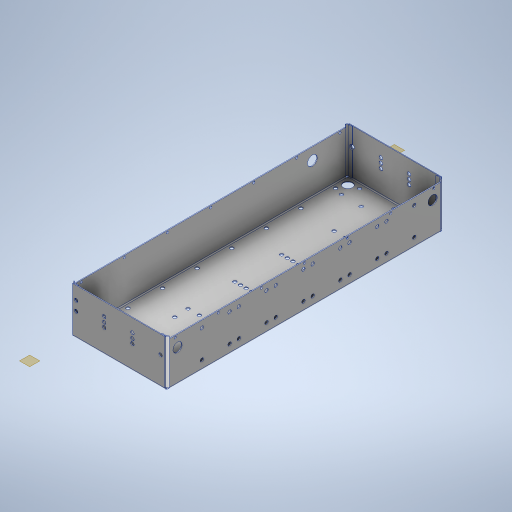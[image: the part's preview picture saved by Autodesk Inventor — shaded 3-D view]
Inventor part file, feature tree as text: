
AUTODESK INVENTOR PART (.ipt)
format: ipt  version: 2023 (Build 270158000, 158)  size: 787,968 bytes
history: native  units: in
note: dims shown in document units (in); Inventor stores cm internally (conversion verified against a paired STEP export)
features: sketch x26, hole x20, sheet_metal_op x12, pattern_linear x12, other x8, plane x4
ambient origin geometry x8: Origin, YZ Plane, XZ Plane, XY Plane, X Axis, Y Axis, Z Axis, Center Point
bodies: Solid1 (feature_tree)
feature tree (82):
  sheet_metal_op  "Face1"
  sheet_metal_op  "Flange1"
  sheet_metal_op  "Flange2"
  sheet_metal_op  "Unfold1"
  hole  "Hole1"  [1 undecoded]
  pattern_linear  "Rectangular Pattern1"  Count1=30  [1 undecoded]
  pattern_linear  "Rectangular Pattern2"  Count1=10  [1 undecoded]
  hole  "Hole2"  [1 undecoded]
  pattern_linear  "Rectangular Pattern3"  Count1=10 Spacing1=90.0deg
  hole  "Hole3"  [1 undecoded]
  hole  "Hole6"  [1 undecoded]
  pattern_linear  "Rectangular Pattern6"  Count1=10 Spacing1=90.0deg
  plane  "Work Plane4"
  hole  "Hole7"  [1 undecoded]
  plane  "Work Plane3"
  hole  "Hole8"  [1 undecoded]
  plane  "Work Plane2"
  hole  "Hole9"  [1 undecoded]
  plane  "Work Plane1"
  hole  "Hole10"  [1 undecoded]
  hole  "Hole11"  [1 undecoded]
  hole  "Hole12"  [1 undecoded]
  hole  "Hole13"  [1 undecoded]
  pattern_linear  "Rectangular Pattern11"  Count1=6  [1 undecoded]
  pattern_linear  "Rectangular Pattern12"  Count1=6  [1 undecoded]
  pattern_linear  "Rectangular Pattern13"  Count1=6  [1 undecoded]
  pattern_linear  "Rectangular Pattern14"  Count1=2  [1 undecoded]
  sheet_metal_op  "Refold6"
  sheet_metal_op  "Flange8"
  hole  "Hole14"  [1 undecoded]
  hole  "Hole15"  [1 undecoded]
  hole  "Hole16"  [1 undecoded]
  hole  "Hole17"  [1 undecoded]
  hole  "Hole18"  [1 undecoded]
  hole  "Hole19"  [1 undecoded]
  pattern_linear  "Rectangular Pattern15"  Count1=3  [1 undecoded]
  hole  "Hole20"  [1 undecoded]
  pattern_linear  "Rectangular Pattern16"  Count1=3  [1 undecoded]
  hole  "Hole22"  [1 undecoded]
  pattern_linear  "Rectangular Pattern18"  Count1=3  [1 undecoded]
  hole  "Hole21"  [1 undecoded]
  pattern_linear  "Rectangular Pattern17"  Spacing1=0.374in  [1 undecoded]
  sketch  "Sketch1"  dims[d0=23.622in d1=7.874in d2=11.811in d3=3.937in]
  other  "Plate1"
  sketch  "Sketch2"  dims[d4=0.0625in d5=0.0625in]
  other  "Plate2"
  sheet_metal_op  "Bend1"
  sheet_metal_op  "Corner1"
  sketch  "Sketch3"  dims[d6=0.0312in]
  other  "Plate3"
  sheet_metal_op  "Bend2"
  sheet_metal_op  "Corner2"
  sketch  "Sketch5"  dims[d7=0.125in]
  sketch  "Sketch6"  dims[d8=0.0625in d9=3.937in d10=90.0deg d11=0.0787in]
  sketch  "Sketch7"  dims[d12=0.25in d13=0.0625in]
  sketch  "Sketch10"  dims[d14=0.0625in d15=0.0625in]
  sketch  "Sketch11"  dims[d16=0.0312in]
  sketch  "Sketch13"  dims[d17=0.125in]
  sketch  "Sketch15"  dims[d18=0.0625in d19=3.937in d20=90.0deg d21=0.0787in]
  sketch  "Sketch16"  dims[d22=0.25in d23=0.0625in]
  sketch  "Sketch17"  dims[d24=0.0625in]
  sketch  "Sketch21"  dims[d35=0.2969in d36=0.2953in d37=0.1476in d38=0.0984in d39=90.0deg d40=0.0625in d41=0.8108in]
  sketch  "Sketch25"  dims[d42=0.7874in d44=0.9646in d46=1.1811in d48=3.9921in]
  sketch  "Sketch26"  dims[d49=0.2969in d50=0.2953in d51=0.1476in d52=0.0984in d53=90.0deg d54=0.3937in d55=0.8108in d56=0.9646in]
  other  "Plate9"
  sheet_metal_op  "Bend8"
  sheet_metal_op  "Corner8"
  sketch  "Sketch27"  dims[d57=0.9646in d58=0.4823in]
  sketch  "Sketch28"  dims[d59=1.1811in d61=3.9921in]
  sketch  "Sketch29"  dims[d62=0.7874in d63=0.2953in d64=0.1476in d65=0.0984in d66=90.0deg d67=0.3937in d68=0.8108in d69=0.5906in]
  sketch  "Sketch30"  dims[d70=0.5906in]
  sketch  "Sketch31"  dims[d95=0.2969in d96=0.2953in d97=0.1476in d98=0.0984in d99=90.0deg d100=0.0625in d101=0.8108in d102=2.3622in d103=2.3622in d104=2.3622in d105=0.7874in]
  sketch  "Sketch32"  dims[d106=2.3622in d107=2.3622in d109=3.1496in]
  sketch  "Sketch33"  dims[d110=0.2969in d111=0.2953in d112=0.1476in d113=0.0984in d114=90.0deg d115=0.0625in d116=0.8108in]
  sketch  "Sketch34"  dims[d122=0.2969in d123=0.2953in d124=0.1476in d125=0.0984in d126=90.0deg d127=0.3937in d128=0.8108in d129=0.8071in]
  sketch  "Sketch35"  dims[d130=0.4035in]
  sketch  "Sketch36"  dims[d134=0.2969in d135=0.2953in d136=0.1476in d137=0.0984in d138=90.0deg d139=0.3937in d140=0.8108in]
  sketch  "Sketch37"  dims[d144=0.2969in d145=0.2953in d146=0.1476in d147=0.0984in d148=90.0deg d149=0.3937in d150=0.8108in d151=0.8071in d158=0.2969in d159=0.2953in d160=0.1476in d161=0.0984in d162=90.0deg d163=0.3937in d164=0.8108in d165=1.9252in d166=2.6949in d167=1.1811in d168=0.9626in d169=0.7874in d170=0.2953in d171=0.1476in d172=0.0984in d173=90.0deg d174=0.3937in d175=0.8108in d176=0.7874in d177=0.2953in d178=0.1476in d179=0.0984in d180=90.0deg d181=0.3937in d182=0.8108in d183=1.1811in d184=0.7874in d185=1.1811in d186=0.7874in d188=0.374in d189=2.433in d190=0.3346in d191=2.433in d192=1.1811in d194=2.4016in d195=1.1811in d197=2.4016in d198=1.1811in d200=2.4016in d201=1.1811in d203=2.4016in d205=7.0866in d206=0.5316in d231=0.0984in d250=0.0in d263=0.0in d265=0.0in d271=0.0625in d272=0.0in d273=0.0625in d274=0.0in d275=0.0625in d276=0.0312in d277=0.125in d278=0.0625in d279=0.5in d280=90.0deg d281=0.0984in d282=0.25in d283=0.0625in d284=0.0625in d285=7.874in d286=2.4016in d287=0.4331in d288=0.2953in d289=0.1476in d290=0.0984in d291=90.0deg d292=0.0625in d293=0.0in d294=0.4331in d295=0.2953in d296=0.1476in d297=0.0984in d298=90.0deg d299=0.3937in d300=0.0in d301=0.8386in d302=0.2953in d303=0.1476in d304=0.0984in d305=90.0deg d306=0.0625in d307=0.8108in d308=0.2969in d309=0.2953in d310=0.1476in d311=0.0984in d312=90.0deg d313=0.3937in d314=0.8108in d316=2.2441in d319=0.2969in d320=0.2953in d321=0.1476in d322=0.0984in d323=90.0deg d324=0.3937in d325=0.8108in d326=1.0236in d327=1.5748in d328=2.9528in d329=2.5591in d330=1.0236in d331=2.7559in d332=0.5906in d333=0.0in d334=0.2969in d335=0.2953in d336=0.1476in d337=0.0984in d338=90.0deg d339=0.0625in d340=0.8108in d341=0.5in d342=1.5in d343=3.1496in d345=2.9528in d346=0.7874in d348=7.2065in d349=0.2969in d350=0.2953in d351=0.1476in d352=0.0984in d353=90.0deg d354=0.0625in d355=0.8108in d356=0.5in d357=1.5in d358=1.1811in d360=2.9528in d361=0.7874in d363=22.622in d364=0.194in d365=0.2953in d366=0.1476in d367=0.0984in d368=90.0deg d369=0.0625in d370=0.8108in d371=0.5in d372=2.7559in d374=3.6755in d376=0.2073in d377=0.0625in d378=0.0in d379=0.194in d380=0.2953in d381=0.1476in d382=0.0984in d383=90.0deg d384=0.0625in d385=0.8108in d386=0.5in d387=0.162in d388=2.7559in d390=3.6755in d391=0.2073in d392=0.0625in d393=0.0in d394=0.162in]
  other  "Cut4"
  other  "Cut5"
  other  "Cut6"
  other  "Cut7"
note: 30 required parameter values undecoded (feature->parameter linkage not recoverable at this tier; creation-order binding heuristic only, values carry confidence <= 0.55)
